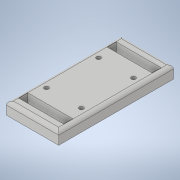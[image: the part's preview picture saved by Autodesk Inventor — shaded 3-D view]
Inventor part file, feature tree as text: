
AUTODESK INVENTOR PART (.ipt)
format: ipt  version: 2022 (Build 260153000, 153)  size: 137,728 bytes
history: native  units: mm
features: sketch x3, extrude x2, hole x1, fillet x1
ambient origin geometry x8: Origin, YZ Plane, XZ Plane, XY Plane, X Axis, Y Axis, Z Axis, Center Point
bodies: Solid1 (feature_tree)
feature tree (7):
  extrude  "Extrusion1"  Depth=65.85mm
  extrude  "Extrusion2"  Depth=25.64mm
  hole  "Hole1"  [1 undecoded]
  fillet  "Fillet1"  Radius=10.0mm
  sketch  "Sketch1"  dims[d0=30.0mm d1=65.85mm]
  sketch  "Sketch2"  dims[d2=7.0mm d3=0.0mm d4=25.64mm]
  sketch  "Sketch3"  dims[d5=5.2mm d6=5.0mm d7=10.0mm d8=0.0mm d9=29.85mm d10=20.0mm d11=2.46mm d12=6.0mm d13=4.0mm d14=2.0mm d15=90.0deg d16=8.0mm d17=0.0mm d18=2.0mm]
note: 1 required parameter value undecoded (feature->parameter linkage not recoverable at this tier; creation-order binding heuristic only, values carry confidence <= 0.55)
